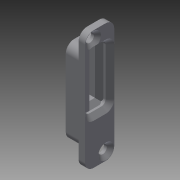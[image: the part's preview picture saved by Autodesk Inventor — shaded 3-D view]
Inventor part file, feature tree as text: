
AUTODESK INVENTOR PART (.ipt)
format: ipt  version: 2013 (Build 170138000, 138)  size: 196,608 bytes
history: native  units: in
note: dims shown in document units (in); Inventor stores cm internally (conversion verified against a paired STEP export)
features: extrude x3, chamfer x3, sketch x3
ambient origin geometry x8: Origin, YZ Plane, XZ Plane, XY Plane, X Axis, Y Axis, Z Axis, Center Point
bodies: Solid1 (feature_tree)
feature tree (9):
  extrude  "Extrusion1"  Depth=0.2677in
  chamfer  "Chamfer1"  Distance=0.0591in
  extrude  "Extrusion2"  Depth=0.0394in
  extrude  "Extrusion3"  Depth=0.0591in TaperAngle=0.0deg
  chamfer  "Chamfer2"  Distance=0.2677in
  chamfer  "Chamfer3"  Distance=0.7795in
  sketch  "Sketch1"  dims[d0=1.0945in d1=0.2677in]
  sketch  "Sketch2"  dims[d2=0.0787in d3=0.0591in d4=0.0in]
  sketch  "Sketch3"  dims[d6=0.0315in d7=0.0787in d8=45.0deg d11=0.0394in d12=0.0591in d13=0.0in d14=0.2677in d15=0.7795in d16=0.0787in d17=0.1181in d18=0.0in d19=0.0394in d20=0.5118in d21=0.0394in d22=0.0394in d23=0.0394in d24=0.0394in d25=0.4134in d26=0.0394in d27=0.0787in d28=45.0deg d29=0.0394in d30=0.0984in d31=0.0394in d32=0.0512in d33=0.0394in d34=0.0394in d35=0.0394in d36=0.0787in d37=45.0deg d38=0.0787in d39=0.0039in d40=0.0039in]
